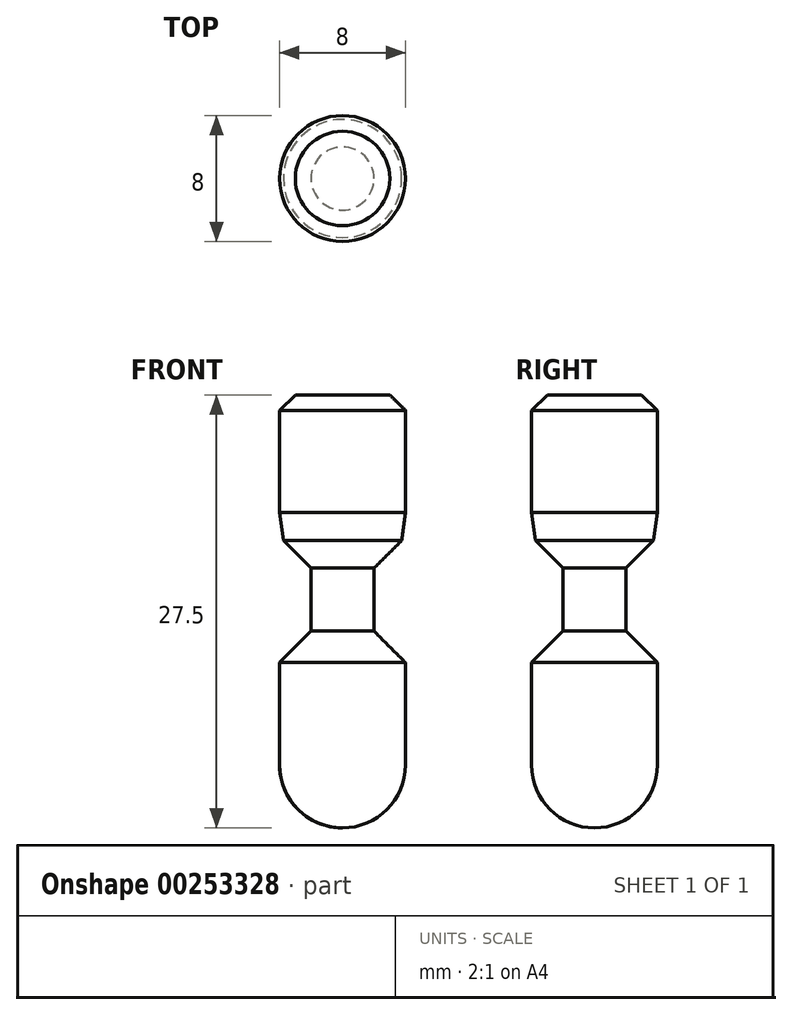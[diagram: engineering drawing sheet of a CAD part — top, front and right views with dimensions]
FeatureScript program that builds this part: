
annotation { "Feature Type Name" : "Feature", "Feature Type Description" : "" }
export const myFeature = defineFeature(function(context is Context, id is Id, definition is map)
    precondition{}
    {
        {
            var Q0;
            Q0=qCreatedBy(makeId("Front.planeOp"),FACE);
            var sketch = newSketch(context, id + "F0", { "sketchPlane" : qUnion([Q0])});
            skLineSegment(sketch, "E0", {"start": v(0, 27.98) * mm, "end": v(0, -12.05) * mm, "construction": true});
            skLineSegment(sketch, "E1", {"start": v(0, 23.5) * mm, "end": v(3, 23.5) * mm});
            skLineSegment(sketch, "E2", {"start": v(3, 23.5) * mm, "end": v(4, 22.53) * mm});
            skLineSegment(sketch, "E3", {"start": v(4, 22.53) * mm, "end": v(4, 16.03) * mm});
            skLineSegment(sketch, "E4", {"start": v(4, 16.03) * mm, "end": v(3.75, 14.25) * mm});
            skLineSegment(sketch, "E5", {"start": v(3.75, 14.25) * mm, "end": v(2, 12.5) * mm});
            skLineSegment(sketch, "E6", {"start": v(2, 12.5) * mm, "end": v(2, 8.5) * mm});
            skLineSegment(sketch, "E7", {"start": v(2, 8.5) * mm, "end": v(4, 6.5) * mm});
            skLineSegment(sketch, "E8", {"start": v(4, 6.5) * mm, "end": v(4, 0) * mm});
            skLineSegment(sketch, "E9", {"start": v(4, 0) * mm, "end": v(0, 0) * mm});
            skLineSegment(sketch, "E10", {"start": v(0, 0) * mm, "end": v(0, 23.5) * mm});
            skLineSegment(sketch, "E11.MirrorCS", {"start": v(-4, 16.03) * mm, "end": v(-3.75, 14.25) * mm, "construction": true});
            skLineSegment(sketch, "E12.MirrorCS", {"start": v(-3.75, 14.25) * mm, "end": v(-2, 12.5) * mm, "construction": true});
            skLineSegment(sketch, "E13.MirrorCS", {"start": v(-4, 6.5) * mm, "end": v(-4, 0) * mm, "construction": true});
            skLineSegment(sketch, "E14.MirrorCS", {"start": v(-2, 8.5) * mm, "end": v(-4, 6.5) * mm, "construction": true});
            skLineSegment(sketch, "E15.MirrorCS", {"start": v(-3, 23.5) * mm, "end": v(-4, 22.53) * mm, "construction": true});
            skLineSegment(sketch, "E16.MirrorCS", {"start": v(-2, 12.5) * mm, "end": v(-2, 8.5) * mm, "construction": true});
            skLineSegment(sketch, "E17.MirrorCS", {"start": v(-4, 22.53) * mm, "end": v(-4, 16.03) * mm, "construction": true});
            skLineSegment(sketch, "E18.MirrorCS", {"start": v(0, 23.5) * mm, "end": v(-3, 23.5) * mm, "construction": true});
            skLineSegment(sketch, "E19.MirrorCS", {"start": v(-4, 0) * mm, "end": v(0, 0) * mm, "construction": true});
            skArc(sketch, "E20", {"start": v(-4, 0) * mm, "mid": v(0, -4) * mm, "end": v(4, 0) * mm});
            skPoint(sketch, "E21", {"position": v(0, -4) * mm});
            skLineSegment(sketch, "E22", {"start": v(0, 0) * mm, "end": v(0, -4) * mm});
            skSolve(sketch);
        }
        {
            var Q0;
            Q0=makeQuery(id+"F0.imprint","IMPRINT",FACE,{"disambiguationData":[TD([[makeQuery(id+"F0.imprint","IMPRINT",EDGE,{"derivedFrom":sQuery(id+"F0.wireOp",EDGE,"E1")}),-1.0]])]});
            var Q1;
            Q1=sQuery(id+"F0.wireOp",EDGE,"E0");
            revolve(context, id + "F1", {"entities" : qUnion([Q0]), "axis" : qUnion([Q1]), "revolveType" : RevolveType.FULL});
        }
        {
            var Q0;
            {var subQ0=sQuery(id+"F0.wireOp",EDGE,"E9");Q0=makeQuery(id+"F0.imprint","IMPRINT",FACE,{"disambiguationData":[TD([[makeQuery(id+"F0.imprint","IMPRINT",EDGE,{"derivedFrom":subQ0}),1.0]])]});}
            var Q1;
            Q1=sQuery(id+"F0.wireOp",EDGE,"E0");
            revolve(context, id + "F2", {"operationType" : NewBodyOperationType.ADD, "entities" : qUnion([Q0]), "axis" : qUnion([Q1]), "revolveType" : RevolveType.FULL});
        }
    });
